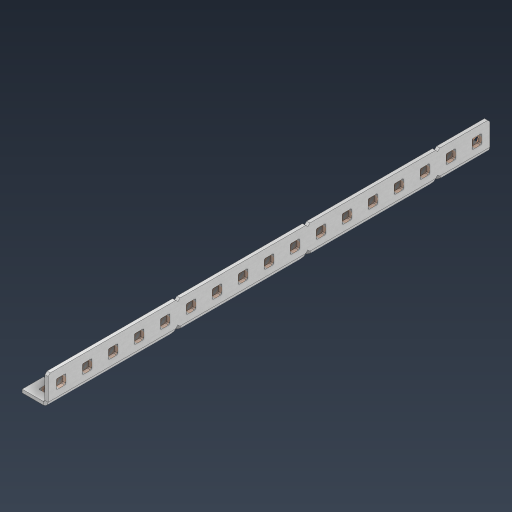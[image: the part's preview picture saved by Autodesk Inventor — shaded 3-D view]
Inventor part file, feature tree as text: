
AUTODESK INVENTOR PART (.ipt)
format: ipt  version: 2024.3 (Build 283343000, 343)  size: 779,264 bytes
history: native  units: in
note: dims shown in document units (in); Inventor stores cm internally (conversion verified against a paired STEP export)
features: other x58, extrude x49, sheet_metal_op x11, pattern_linear x2, mirror x1, chamfer x1, sketch x1
ambient origin geometry x8: Origin, YZ Plane, XZ Plane, XY Plane, X Axis, Y Axis, Z Axis, Center Point
bodies: Solid1 (feature_tree), Body (feature_tree)
feature tree (123):
  sheet_metal_op  "Flanges"
  other  "Flange Pattern Plane"
  other  "Flange Pattern Sketch"
  sheet_metal_op  "Flange Pattern"
  sheet_metal_op  "Body Pattern"
  pattern_linear  "Center Pattern"  Spacing1=8.5in  [1 undecoded]
  other  "Arc Length"
  mirror  "Notch Mirror"
  pattern_linear  "Notch Pattern"  Spacing1=0.0625in  [1 undecoded]
  chamfer  "End Chamfer"
  extrude  "Half Cut"  Depth=0.0625in
  other  "Plate1"
  sketch  "Sketch2"  dims[d0=1.0in d1=8.5in d2=0.0625in d3=0.0625in d4=0.0312in d5=0.125in d6=0.0625in d7=0.5in d8=90.0deg d9=0.0312in d10=0.25in d11=0.0625in d12=0.0625in d16=0.182in d17=0.02in d18=0.0625in d19=0.0in d20=0.25in d21=0.25in d38=6.6929in d40=0.5in d41=0.3937in d43=1.0in d46=0.172in d47=1.0in d48=0.0in d49=0.182in d50=0.02in d51=0.25in d52=0.25in d53=0.0625in d54=0.0in d55=0.172in d56=1.0in d57=0.0in d58=0.25in d60=6.6929in d62=0.5in d63=0.3937in d65=0.5in d85=0.1473in d86=0.1782in d88=0.04in d89=0.0625in d90=0.0in d91=0.04in d92=0.0491in d95=2.5in d96=0.04in d97=0.25in d98=45.0deg d99=0.25in d100=0.5in d101=0.0in d102=2.497in d106=0.182in d107=0.02in d108=0.5in d109=0.5in d110=0.0625in d111=0.0in d112=0.172in d113=0.5in d114=0.0in d117=0.5in d118=0.5in d119=0.5in]
  other  "Plate2"
  sheet_metal_op  "Bend1"
  sheet_metal_op  "Corner1"
  other  "Srf1"
  other  "Srf2"
  other  "Srf91"
  sheet_metal_op  "Body Pattern Sketch"
  other  "Srf92"
  other  "Srf786"
  other  "Srf823"
  other  "Srf824"
  other  "Srf825"
  other  "Srf826"
  other  "Srf827"
  other  "Srf828"
  other  "Srf829"
  other  "Srf856"
  other  "Srf857"
  other  "Srf858"
  other  "Srf859"
  other  "Srf860"
  other  "Srf861"
  other  "Srf862"
  other  "Srf889"
  other  "Srf890"
  other  "Srf891"
  other  "Srf892"
  other  "Srf893"
  other  "Srf894"
  other  "Srf895"
  other  "Srf896"
  other  "Srf922"
  other  "Srf923"
  other  "Srf924"
  other  "Srf925"
  other  "Srf926"
  other  "Srf959"
  other  "Srf960"
  other  "Srf961"
  other  "Srf962"
  other  "Srf963"
  other  "Srf996"
  other  "Srf997"
  other  "Srf998"
  other  "Srf999"
  other  "Srf1000"
  other  "Srf1143"
  other  "Srf1144"
  other  "Srf1145"
  other  "Srf1199"
  other  "Srf1200"
  other  "Srf1201"
  other  "Srf1255"
  other  "Srf1256"
  other  "Srf1257"
  sheet_metal_op  "Flange Stamp"
  sheet_metal_op  "Flange Circle"
  sheet_metal_op  "Body Stamp"
  sheet_metal_op  "Body Circle"
  other  "Center Stamp"
  other  "Center Circle"
  sheet_metal_op  "Notch"
  extrude  "ExtrusionSrf2"  Depth=0.0312in
  extrude  "ExtrusionSrf92"  Depth=0.5in
  extrude  "ExtrusionSrf823"  Depth=0.0625in
  extrude  "ExtrusionSrf824"  Depth=0.5in TaperAngle=90.0deg
  extrude  "ExtrusionSrf825"  Depth=0.5in
  extrude  "ExtrusionSrf826"  Depth=0.0625in
  extrude  "ExtrusionSrf827"  Depth=0.0625in
  extrude  "ExtrusionSrf828"  Depth=0.182in
  extrude  "ExtrusionSrf829"  Depth=0.02in
  extrude  "ExtrusionSrf856"  Depth=0.0625in
  extrude  "ExtrusionSrf857"  TaperAngle=0.0deg  [1 undecoded]
  extrude  "ExtrusionSrf858"  Depth=0.5in
  extrude  "ExtrusionSrf859"  Depth=0.5in
  extrude  "ExtrusionSrf860"  Depth=0.5in
  extrude  "ExtrusionSrf861"  Depth=0.5in
  extrude  "ExtrusionSrf862"  Depth=1.0in TaperAngle=0.0deg
  extrude  "ExtrusionSrf889"  Depth=0.182in
  extrude  "ExtrusionSrf890"  Depth=0.02in
  extrude  "ExtrusionSrf891"  Depth=0.5in
  extrude  "ExtrusionSrf892"  Depth=0.5in
  extrude  "ExtrusionSrf893"  Depth=0.0625in
  extrude  "ExtrusionSrf894"  TaperAngle=0.0deg  [1 undecoded]
  extrude  "ExtrusionSrf895"  Depth=0.5in
  extrude  "ExtrusionSrf896"  Depth=1.0in TaperAngle=0.0deg
  extrude  "ExtrusionSrf922"  Depth=0.5in
  extrude  "ExtrusionSrf923"  Depth=0.5in
  extrude  "ExtrusionSrf924"  Depth=0.5in
  extrude  "ExtrusionSrf925"  Depth=0.5in
  extrude  "ExtrusionSrf926"  Depth=0.5in
  extrude  "ExtrusionSrf959"  Depth=0.5in
  extrude  "ExtrusionSrf960"  Depth=0.0625in
  extrude  "ExtrusionSrf961"  TaperAngle=0.0deg  [1 undecoded]
  extrude  "ExtrusionSrf962"  Depth=0.5in
  extrude  "ExtrusionSrf963"  Depth=0.5in
  extrude  "ExtrusionSrf996"  Depth=0.5in
  extrude  "ExtrusionSrf997"  Depth=0.5in TaperAngle=45.0deg
  extrude  "ExtrusionSrf998"  Depth=0.5in
  extrude  "ExtrusionSrf999"  Depth=0.5in TaperAngle=0.0deg
  extrude  "ExtrusionSrf1000"  Depth=0.5in
  extrude  "ExtrusionSrf1143"  Depth=0.182in
  extrude  "ExtrusionSrf1144"  Depth=0.02in
  extrude  "ExtrusionSrf1145"  Depth=0.5in
  extrude  "ExtrusionSrf1199"  Depth=0.5in
  extrude  "ExtrusionSrf1200"  Depth=0.0625in
  extrude  "ExtrusionSrf1201"  TaperAngle=0.0deg  [1 undecoded]
  extrude  "ExtrusionSrf1255"  Depth=0.5in
  extrude  "ExtrusionSrf1256"  Depth=0.5in TaperAngle=0.0deg
  extrude  "ExtrusionSrf1257"  Depth=0.5in
note: 6 required parameter values undecoded (feature->parameter linkage not recoverable at this tier; creation-order binding heuristic only, values carry confidence <= 0.55)
